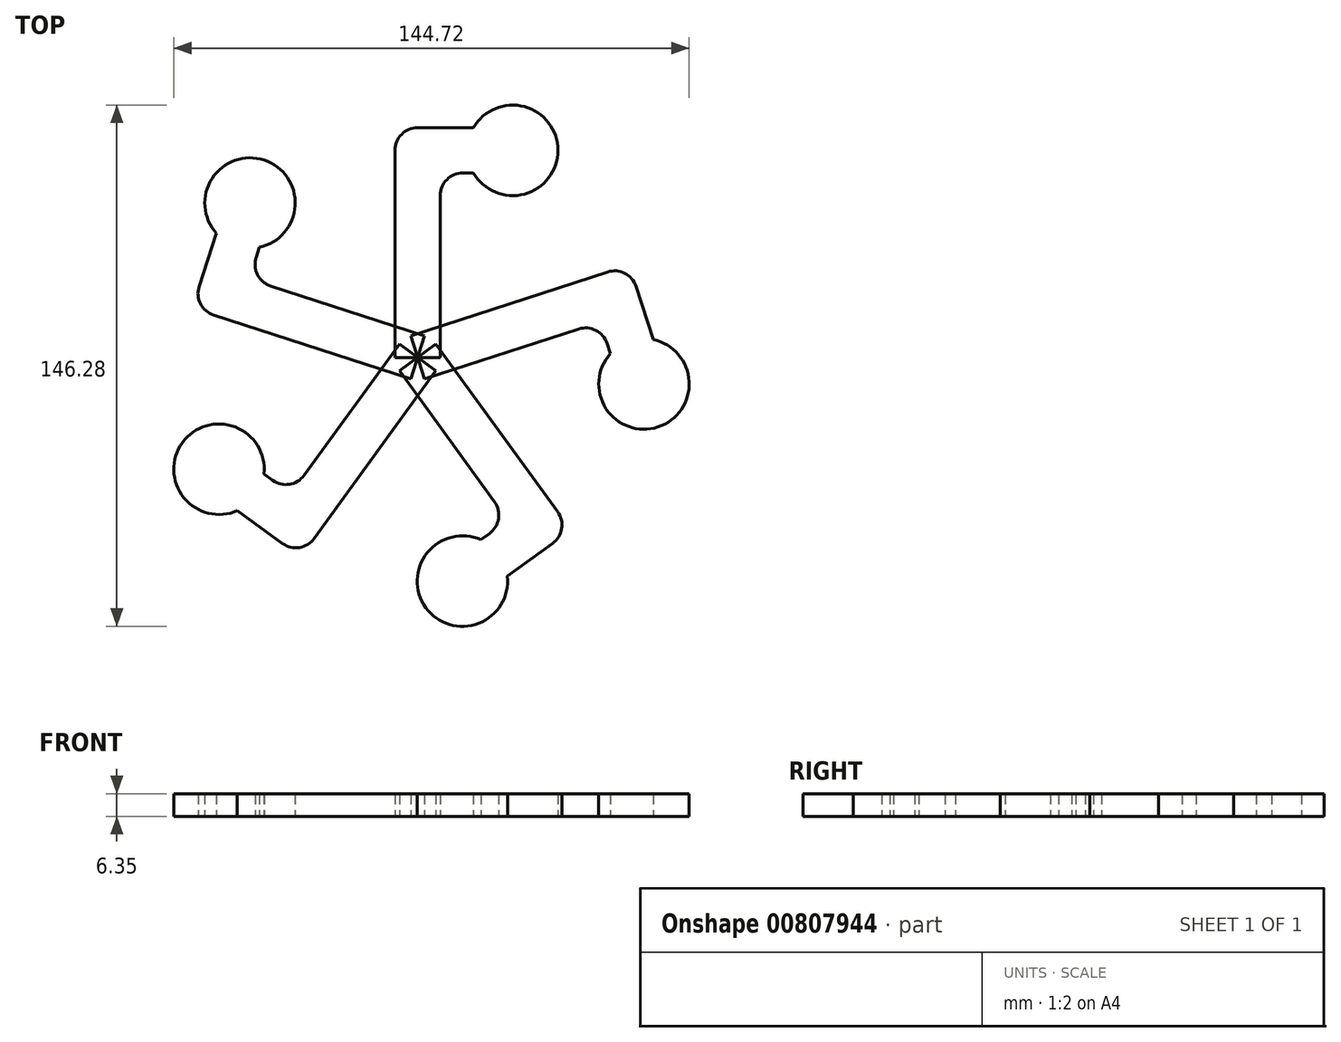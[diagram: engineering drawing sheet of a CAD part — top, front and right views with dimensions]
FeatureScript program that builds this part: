
annotation { "Feature Type Name" : "Feature", "Feature Type Description" : "" }
export const myFeature = defineFeature(function(context is Context, id is Id, definition is map)
    precondition{}
    {
        {
            var Q0;
            Q0=qCreatedBy(makeId("Top.planeOp"),FACE);
            var sketch = newSketch(context, id + "F0", { "sketchPlane" : qUnion([Q0])});
            skLineSegment(sketch, "E0.0", {"start": v(12.7, 51.8) * mm, "end": v(15.7, 51.8) * mm});
            skLineSegment(sketch, "E1.0", {"start": v(6.35, 0) * mm, "end": v(6.35, 45.45) * mm});
            skLineSegment(sketch, "E2.0", {"start": v(-6.35, 0) * mm, "end": v(-6.35, 58.15) * mm});
            skLineSegment(sketch, "E3.0", {"start": v(0, 64.5) * mm, "end": v(15.7, 64.5) * mm});
            skArc(sketch, "E4.filletArc", {"start": v(0, 64.5) * mm, "mid": v(-4.5, 62.64) * mm, "end": v(-6.35, 58.15) * mm});
            skArc(sketch, "E5.filletArc", {"start": v(12.7, 51.8) * mm, "mid": v(8.2, 49.94) * mm, "end": v(6.35, 45.45) * mm});
            skLineSegment(sketch, "E6", {"start": v(-6.35, 0) * mm, "end": v(6.35, 0) * mm});
            skPoint(sketch, "E7", {"position": v(26.69, 58.15) * mm});
            skCircle(sketch, "E8", {"center": v(26.69, 58.15) * mm, "radius": 12.7 * mm});
            skSolve(sketch);
        }
        {
            var Q0;
            Q0=qSketchRegion(id+"F0",true);
            extrude(context, id + "F1", {"entities" : qUnion([Q0]), "depth" : 6.35 * mm, "offsetDistance" : 25.4 * mm});
        }
        {
            var Q0;
            Q0=qCreatedBy(makeId("Right.planeOp"),FACE);
            var sketch = newSketch(context, id + "F2", { "sketchPlane" : qUnion([Q0])});
            skLineSegment(sketch, "E9", {"start": v(0, 0) * mm, "end": v(0, 49.57) * mm});
            skSolve(sketch);
        }
        {
            var Q0;
            Q0=makeQuery(id+"F1.opExtrude","SWEPT_BODY",BODY,{"disambiguationData":[OSD([sQuery(id+"F0.wireOp",EDGE,"QuxXVNvQ-RgSI-eEx2-24oe-8oqEmTtYgdey"),sQuery(id+"F0.wireOp",EDGE,"E0.0"),sQuery(id+"F0.wireOp",EDGE,"E1.0"),sQuery(id+"F0.wireOp",EDGE,"E2.0"),sQuery(id+"F0.wireOp",EDGE,"E3.0"),sQuery(id+"F0.wireOp",EDGE,"E4.filletArc"),sQuery(id+"F0.wireOp",EDGE,"E5.filletArc"),sQuery(id+"F0.wireOp",EDGE,"E6")])]});
            var Q1;
            Q1=sQuery(id+"F2.wireOp",EDGE,"E9");
            circularPattern(context, id + "F3", {"entities" : qUnion([Q0]), "axis" : qUnion([Q1]), "angle" : 360 * degree, "instanceCount" : 5, "equalSpace" : true});
        }
    });
